# Revit family: Grinder_Pump-Hazardous_Environment-Zoeller-X840_Seriesxxx
name_source: partatom
category: Mechanical Equipment
revit_build: Autodesk Revit 2014 (Build: 20130308_1515(x64)
units: mm (PartAtom-declared; Revit-internal decimal feet)

## types (6) — shared parameters
Adapter = Cast iron
Assembly Code = D2090
Cap = Cast iron
Cooling = Oil filled
Cord Length = 240"
Cord Type = UL listed, SOOW
Cutter = Hardened stainless steel, Rockwell C55-60
Default Elevation = 0"
Description = Hazardous Location Grinder Pump With Explosion-Proof Motors
Discharge Diameter = 1 1/4"
Discharge Height = 5 3/8"
Discharge Radius = 5/8"
Flow @ 5' = 45 GPM
Hardware = Stainless steel
Hertz = 60
Horse Power = 2
Impeller = Ductile iron or bronze
Impeller Type = Non-clogging vortex
Installation Type = Floor Mounted
Insulation = Class F
Length = 11 27/32"
Lower Bearing = Ball bearing
Manufacturer = Zoeller
Material = Cast Iron-Zoeller-Powder Coated Epoxy
Max Flow Rate = 59 GPM (223 LPM)
Max. Head = 104 ft (31.7m)
Max. Operating Temp. = 104° F (40° C)
Mechanical Seals = Carbon/ceramic with stainless steel parts
Motor Housing = Cast iron
Motor Shaft = Stainless steel
Operation = Non-Automatic
Overall Height = 26 31/32"
Price = Prices may vary. Please consult Manufacturer Representative for most up-to-date price list.
Product Documentation Link = http://cdn.qleapahead.com
Product Page URL = http://www.zoellerpumps.com
Pump Housing = Cast iron
RPM = 3450
Shipping Weight = 155 Lbs.
Square Rings = Neoprene
URL = http://www.zoellerengprod.com
Upper Bearing = Ball bearing
Warranty Information = 36 Months (Limited)
Waste Connection = Yes
Width = 8 1/2"

## per-type parameters (varying)
| type | Amps | Apparent Load | Model | Motor Protection | Phase | Type | Voltage |
| IX840-1.25" 200V/1Ph/20A/2HP | 20 A | 4000 VA | IX840 | Auto reset thermal overload | 1 | Capacitor start / capacitor run | 200 V |
| EX840-1.25" 230V/1Ph/17.2A/2HP | 17 A | 3956 VA | EX840 | Auto reset thermal overload | 1 | Capacitor start / capacitor run | 230 V |
| JX840-1.25" 200V/3Ph/12.3A/2HP | 12 A | 2460 VA | JX840 | Thermal Sensor | 3 | 3 Ph | 200 V |
| FX840-1.25" 230V/3Ph/10.8A/2HP | 11 A | 2484 VA | FX840 | Thermal Sensor | 3 | 3 Ph | 230 V |
| GX840-1.25" 460V/3Ph/5.5A/2HP | 6 A | 2530 VA | GX840 | Thermal Sensor | 3 | 3 Ph | 460 V |
| BAX840-1.25" 575V/3Ph/4.5A/2HP | 5 A | 2588 VA | BAX840 | Thermal Sensor | 3 | 3 Ph | 575 V |

## geometry (parser evidence)
native form markers: Blend x4, Sweep x1
no freeform markers — native parametric forms only
